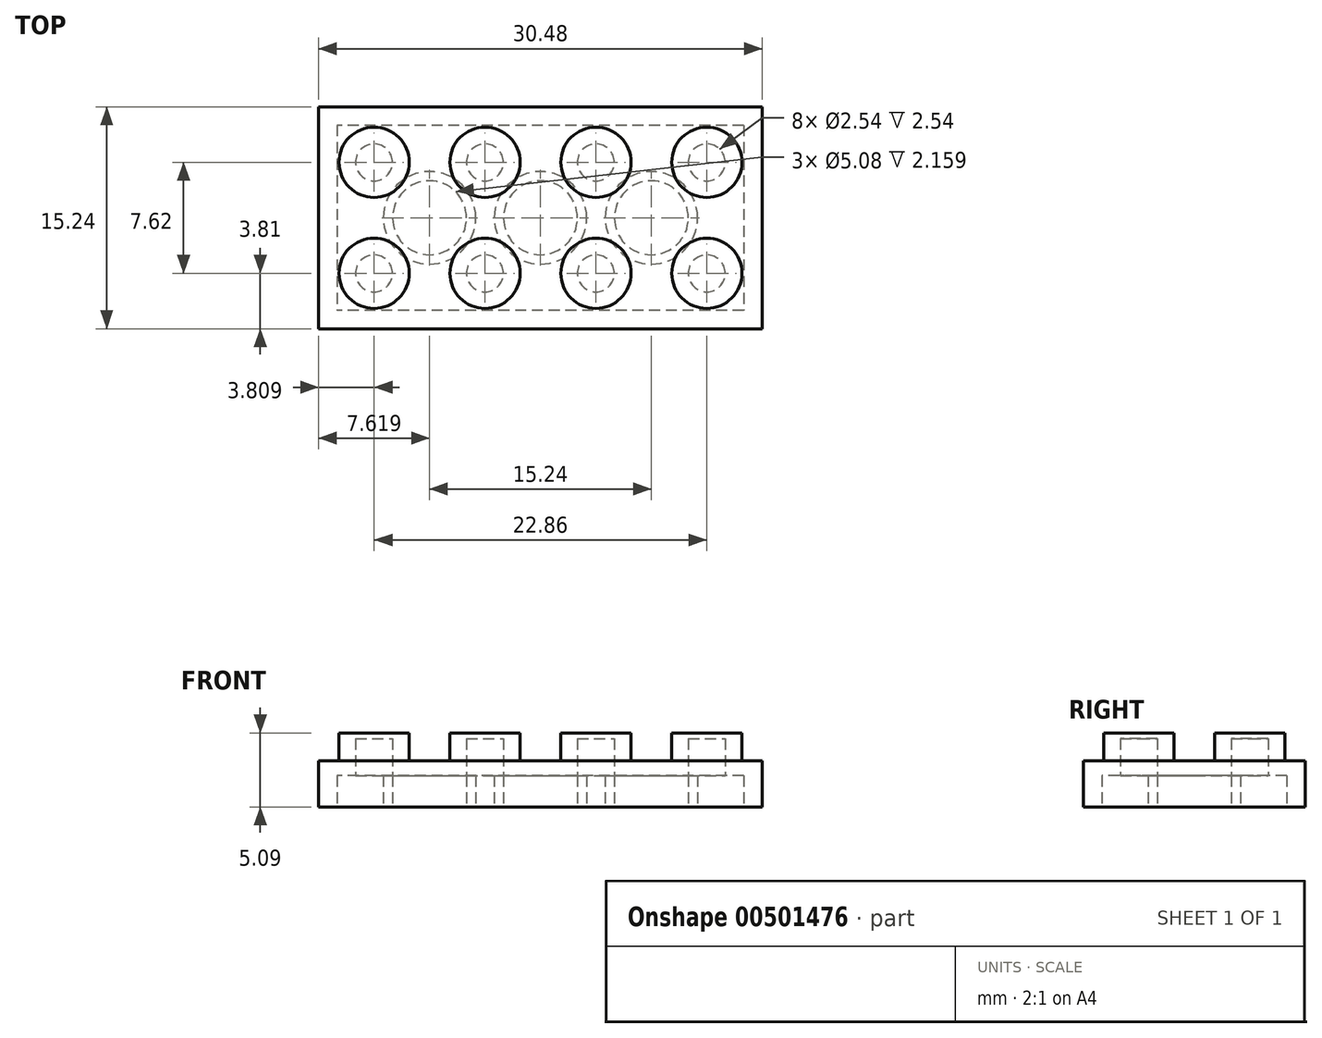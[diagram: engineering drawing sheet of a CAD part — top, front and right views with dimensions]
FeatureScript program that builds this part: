
annotation { "Feature Type Name" : "Feature", "Feature Type Description" : "" }
export const myFeature = defineFeature(function(context is Context, id is Id, definition is map)
    precondition{}
    {
        {
            var Q0;
            Q0=qCreatedBy(makeId("Top.planeOp"),FACE);
            var sketch = newSketch(context, id + "F0", { "sketchPlane" : qUnion([Q0])});
            skLineSegment(sketch, "E0.bottom", {"start": v(-53.47, 28.84) * mm, "end": v(-23, 28.84) * mm});
            skLineSegment(sketch, "E0.top", {"start": v(-53.47, 13.6) * mm, "end": v(-23, 13.6) * mm});
            skLineSegment(sketch, "E0.left", {"start": v(-53.47, 28.84) * mm, "end": v(-53.47, 13.6) * mm});
            skLineSegment(sketch, "E0.right", {"start": v(-23, 28.84) * mm, "end": v(-23, 13.6) * mm});
            skSolve(sketch);
        }
        {
            var Q0;
            Q0=makeQuery(id+"F0.imprint","IMPRINT",FACE,{"disambiguationData":[TD([[makeQuery(id+"F0.imprint","IMPRINT",EDGE,{"derivedFrom":sQuery(id+"F0.wireOp",EDGE,"E0.bottom")}),-1.0]])]});
            var sketch = newSketch(context, id + "F1", { "sketchPlane" : qUnion([Q0])});
            skCircle(sketch, "E1", {"center": v(-26.8, 25.03) * mm, "radius": 2.41 * mm});
            skCircle(sketch, "E2", {"center": v(-26.8, 17.41) * mm, "radius": 2.41 * mm});
            skCircle(sketch, "E3", {"center": v(-34.42, 25.03) * mm, "radius": 2.41 * mm});
            skCircle(sketch, "E4", {"center": v(-34.42, 17.41) * mm, "radius": 2.41 * mm});
            skCircle(sketch, "E5", {"center": v(-42.04, 25.03) * mm, "radius": 2.41 * mm});
            skCircle(sketch, "E6", {"center": v(-42.04, 17.41) * mm, "radius": 2.41 * mm});
            skCircle(sketch, "E7", {"center": v(-49.66, 25.03) * mm, "radius": 2.41 * mm});
            skCircle(sketch, "E8", {"center": v(-49.66, 17.41) * mm, "radius": 2.41 * mm});
            skSolve(sketch);
        }
        {
            var Q0;
            Q0 = qSketchRegion(id + "F0", true);
            extrude(context, id + "F2", {"entities" : qUnion([Q0]), "oppositeDirection" : true, "depth" : 3.17 * mm});
        }
        {
            var Q0;
            Q0 = qSketchRegion(id + "F1", true);
            extrude(context, id + "F3", {"entities" : qUnion([Q0]), "operationType" : NewBodyOperationType.ADD, "depth" : 1.9 * mm});
        }
        {
            var Q0;
            Q0=makeQuery(id+"F2.opExtrude","CAP_FACE",FACE,{"disambiguationData":[OSD([sQuery(id+"F0.wireOp",EDGE,"E0.bottom"),sQuery(id+"F0.wireOp",EDGE,"E0.top"),sQuery(id+"F0.wireOp",EDGE,"E0.left"),sQuery(id+"F0.wireOp",EDGE,"E0.right")])],"isStart":false});
            var sketch = newSketch(context, id + "F4", { "sketchPlane" : qUnion([Q0])});
            skCircle(sketch, "E9", {"center": v(-30.61, -21.22) * mm, "radius": 2.54 * mm});
            skCircle(sketch, "E10", {"center": v(-30.61, -21.22) * mm, "radius": 3.18 * mm});
            skCircle(sketch, "E11", {"center": v(-38.23, -21.22) * mm, "radius": 2.54 * mm});
            skPoint(sketch, "E11.centerSnap0", {"position": v(-38.23, -13.6) * mm});
            skCircle(sketch, "E12", {"center": v(-38.23, -21.22) * mm, "radius": 3.18 * mm});
            skCircle(sketch, "E13", {"center": v(-45.85, -21.22) * mm, "radius": 2.54 * mm});
            skCircle(sketch, "E14", {"center": v(-45.85, -21.22) * mm, "radius": 3.18 * mm});
            skLineSegment(sketch, "E15.bottom", {"start": v(-24.26, -27.57) * mm, "end": v(-52.2, -27.57) * mm});
            skLineSegment(sketch, "E15.top", {"start": v(-24.26, -14.87) * mm, "end": v(-52.2, -14.87) * mm});
            skLineSegment(sketch, "E15.left", {"start": v(-24.26, -27.57) * mm, "end": v(-24.26, -14.87) * mm});
            skLineSegment(sketch, "E15.right", {"start": v(-52.2, -27.57) * mm, "end": v(-52.2, -14.87) * mm});
            skSolve(sketch);
        }
        {
            var Q0;
            Q0=makeQuery(id+"F4.imprint","IMPRINT",FACE,{"disambiguationData":[TD([[makeQuery(id+"F4.imprint","IMPRINT",EDGE,{"derivedFrom":sQuery(id+"F4.wireOp",EDGE,"E15.bottom")}),1.0]])]});
            var sketch = newSketch(context, id + "F5", { "sketchPlane" : qUnion([Q0])});
            skCircle(sketch, "E16", {"center": v(-26.8, -25.03) * mm, "radius": 1.27 * mm});
            skCircle(sketch, "E17", {"center": v(-34.42, -25.03) * mm, "radius": 1.27 * mm});
            skCircle(sketch, "E18", {"center": v(-42.04, -25.03) * mm, "radius": 1.27 * mm});
            skCircle(sketch, "E19", {"center": v(-49.66, -25.03) * mm, "radius": 1.27 * mm});
            skCircle(sketch, "E20", {"center": v(-26.8, -17.41) * mm, "radius": 1.27 * mm});
            skCircle(sketch, "E21", {"center": v(-34.42, -17.41) * mm, "radius": 1.27 * mm});
            skCircle(sketch, "E22", {"center": v(-42.04, -17.41) * mm, "radius": 1.27 * mm});
            skCircle(sketch, "E23", {"center": v(-49.66, -17.41) * mm, "radius": 1.27 * mm});
            skSolve(sketch);
        }
        {
            var Q0;
            Q0 = qSketchRegion(id + "F5", true);
            extrude(context, id + "F6", {"entities" : qUnion([Q0]), "operationType" : NewBodyOperationType.REMOVE, "oppositeDirection" : true, "depth" : 4.7 * mm});
        }
        {
            var Q0;
            Q0 = qSketchRegion(id + "F4", true);
            extrude(context, id + "F7", {"entities" : qUnion([Q0]), "operationType" : NewBodyOperationType.REMOVE, "oppositeDirection" : true, "depth" : 2.16 * mm});
        }
        {
            var Q0;
            Q0=makeQuery(id+"F5.imprint","IMPRINT",FACE,{"disambiguationData":[TD([[makeQuery(id+"F5.imprint","IMPRINT",EDGE,{"derivedFrom":sQuery(id+"F5.wireOp",EDGE,"E19")}),1.0]])]});
            extrude(context, id + "F8", {"entities" : qUnion([Q0]), "operationType" : NewBodyOperationType.ADD, "oppositeDirection" : true, "depth" : 4.7 * mm});
        }
        {
            var Q0;
            Q0=makeQuery(id+"F5.imprint","IMPRINT",FACE,{"disambiguationData":[TD([[makeQuery(id+"F5.imprint","IMPRINT",EDGE,{"derivedFrom":sQuery(id+"F5.wireOp",EDGE,"E19")}),1.0]])]});
            extrude(context, id + "F9", {"entities" : qUnion([Q0]), "operationType" : NewBodyOperationType.REMOVE, "oppositeDirection" : true, "depth" : 4.7 * mm});
        }
        {
            var Q0;
            Q0=makeQuery(id+"F4.imprint","IMPRINT",FACE,{"disambiguationData":[TD([[makeQuery(id+"F4.imprint","IMPRINT",EDGE,{"derivedFrom":sQuery(id+"F4.wireOp",EDGE,"E13")}),1.0]])]});
            var Q1;
            Q1=sQuery(id+"F4.wireOp",EDGE,"E13");
            var Q2;
            Q2=sQuery(id+"F4.wireOp",EDGE,"E11");
            var Q3;
            Q3=sQuery(id+"F4.wireOp",EDGE,"E9");
            extrude(context, id + "F10", {"entities" : qUnion([Q0]), "operationType" : NewBodyOperationType.REMOVE, "surfaceEntities" : qUnion([Q1, Q2, Q3]), "oppositeDirection" : true, "depth" : 2.16 * mm});
        }
        {
            var Q0;
            Q0=makeQuery(id+"F4.imprint","IMPRINT",FACE,{"disambiguationData":[TD([[makeQuery(id+"F4.imprint","IMPRINT",EDGE,{"derivedFrom":sQuery(id+"F4.wireOp",EDGE,"E9")}),1.0]])]});
            extrude(context, id + "F11", {"entities" : qUnion([Q0]), "operationType" : NewBodyOperationType.REMOVE, "oppositeDirection" : true, "depth" : 2.16 * mm});
        }
        {
            var Q0;
            Q0=makeQuery(id+"F4.imprint","IMPRINT",FACE,{"disambiguationData":[TD([[makeQuery(id+"F4.imprint","IMPRINT",EDGE,{"derivedFrom":sQuery(id+"F4.wireOp",EDGE,"E11")}),1.0]])]});
            extrude(context, id + "F12", {"entities" : qUnion([Q0]), "operationType" : NewBodyOperationType.REMOVE, "oppositeDirection" : true, "depth" : 2.16 * mm});
        }
    });
